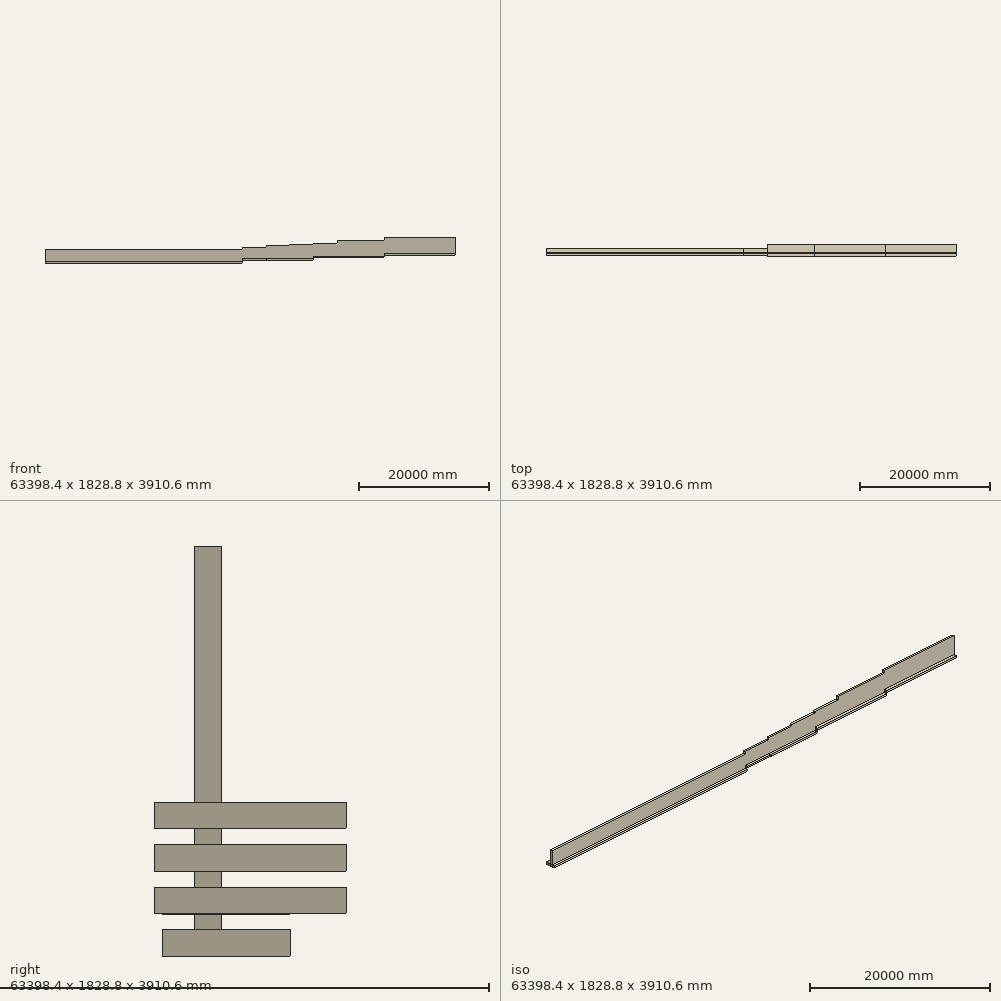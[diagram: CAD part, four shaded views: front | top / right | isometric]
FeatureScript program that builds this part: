
annotation { "Feature Type Name" : "Feature", "Feature Type Description" : "" }
export const myFeature = defineFeature(function(context is Context, id is Id, definition is map)
    precondition{}
    {
        {
            var Q0;
            Q0=qCreatedBy(makeId("Front.planeOp"),FACE);
            var sketch = newSketch(context, id + "F0", { "sketchPlane" : qUnion([Q0])});
            skLineSegment(sketch, "E0.bottom", {"start": v(0, 0) * mm, "end": v(-10972.8, 0) * mm});
            skLineSegment(sketch, "E0.top", {"start": v(0, 2438.4) * mm, "end": v(-10972.8, 2438.4) * mm});
            skLineSegment(sketch, "E0.left", {"start": v(0, 0) * mm, "end": v(0, 2438.4) * mm});
            skLineSegment(sketch, "E0.right", {"start": v(-10972.8, 0) * mm, "end": v(-10972.8, 2438.4) * mm});
            skPoint(sketch, "E1", {"position": v(0, 333.7) * mm});
            skPoint(sketch, "E2", {"position": v(-10972.8, 152.4) * mm});
            skLineSegment(sketch, "E3", {"start": v(-10972.8, 152.4) * mm, "end": v(0, 333.7) * mm, "construction": true});
            skPoint(sketch, "E4", {"position": v(-10972.8, -405.38) * mm});
            skLineSegment(sketch, "E5.left", {"start": v(-10972.8, -405.38) * mm, "end": v(-10972.8, 2033.02) * mm});
            skPoint(sketch, "E6", {"position": v(-33680.4, -643.13) * mm});
            skLineSegment(sketch, "E7", {"start": v(-33680.4, -643.13) * mm, "end": v(-10972.8, 152.4) * mm, "construction": true});
            skPoint(sketch, "E8", {"position": v(-43891.2, -871.73) * mm});
            skLineSegment(sketch, "E9", {"start": v(-43891.2, -871.73) * mm, "end": v(-33680.4, -643.13) * mm, "construction": true});
            skPoint(sketch, "E10", {"position": v(-51511.2, -990.6) * mm});
            skLineSegment(sketch, "E11", {"start": v(-51511.2, -990.6) * mm, "end": v(-43891.2, -871.73) * mm, "construction": true});
            skLineSegment(sketch, "E12.bottom", {"start": v(-51511.2, -990.6) * mm, "end": v(-63398.4, -990.6) * mm, "construction": true});
            skLineSegment(sketch, "E13.bottom", {"start": v(-63398.4, -990.6) * mm, "end": v(-62788.8, -990.6) * mm});
            skPoint(sketch, "E14", {"position": v(-63398.4, 612.65) * mm});
            skPoint(sketch, "E15", {"position": v(-33680.4, 615.7) * mm});
            skLineSegment(sketch, "E16", {"start": v(-63398.4, 612.65) * mm, "end": v(-33680.4, 615.7) * mm, "construction": true});
            skPoint(sketch, "E17", {"position": v(-21945.6, -232.02) * mm});
            skPoint(sketch, "E18", {"position": v(-21945.6, -810.77) * mm});
            skLineSegment(sketch, "E19.bottom", {"start": v(-21945.6, -810.77) * mm, "end": v(-32918.4, -810.77) * mm});
            skPoint(sketch, "E20", {"position": v(-25755.66, 1227.03) * mm});
            skLineSegment(sketch, "E21", {"start": v(-33680.4, 615.7) * mm, "end": v(-25755.66, 1227.03) * mm, "construction": true});
            skPoint(sketch, "E22", {"position": v(-18440.4, 1633.73) * mm});
            skLineSegment(sketch, "E23", {"start": v(-25755.66, 1227.03) * mm, "end": v(-18440.4, 1633.73) * mm, "construction": true});
            skPoint(sketch, "E24", {"position": v(-11125.2, 2039.11) * mm});
            skLineSegment(sketch, "E25", {"start": v(-18440.4, 1633.73) * mm, "end": v(-11125.2, 2039.11) * mm, "construction": true});
            skLineSegment(sketch, "E26", {"start": v(-11125.2, 2039.11) * mm, "end": v(0, 2438.4) * mm, "construction": true});
            skPoint(sketch, "E27", {"position": v(-32918.4, -1216.15) * mm});
            skLineSegment(sketch, "E28.bottom", {"start": v(-32918.4, -1216.15) * mm, "end": v(-63398.4, -1216.15) * mm});
            skLineSegment(sketch, "E28.top", {"start": v(-32918.4, 612.65) * mm, "end": v(-63398.4, 612.65) * mm});
            skLineSegment(sketch, "E28.left", {"start": v(-32918.4, -1216.15) * mm, "end": v(-32918.4, 612.65) * mm});
            skLineSegment(sketch, "E28.right", {"start": v(-63398.4, -1216.15) * mm, "end": v(-63398.4, 612.65) * mm});
            skLineSegment(sketch, "E29.bottom", {"start": v(-10972.8, 2033.02) * mm, "end": v(-18288, 2033.02) * mm});
            skLineSegment(sketch, "E29.top", {"start": v(-10972.8, -405.38) * mm, "end": v(-18288, -405.38) * mm});
            skLineSegment(sketch, "E29.left", {"start": v(-10972.8, 2033.02) * mm, "end": v(-10972.8, -405.38) * mm});
            skLineSegment(sketch, "E29.right", {"start": v(-18288, 2033.02) * mm, "end": v(-18288, -405.38) * mm});
            skLineSegment(sketch, "E30.bottom", {"start": v(-18288, -405.38) * mm, "end": v(-21945.6, -405.38) * mm});
            skLineSegment(sketch, "E30.top", {"start": v(-18288, 1633.73) * mm, "end": v(-21945.6, 1633.73) * mm});
            skLineSegment(sketch, "E30.left", {"start": v(-18288, -405.38) * mm, "end": v(-18288, 1633.73) * mm});
            skLineSegment(sketch, "E30.right", {"start": v(-21945.6, -405.38) * mm, "end": v(-21945.6, 1633.73) * mm});
            skLineSegment(sketch, "E31.right", {"start": v(-21945.6, -809.83) * mm, "end": v(-21945.6, 1438.85) * mm});
            skLineSegment(sketch, "E32.bottom", {"start": v(-21945.6, 1438.85) * mm, "end": v(-25603.2, 1438.85) * mm});
            skLineSegment(sketch, "E32.top", {"start": v(-21945.6, -810.77) * mm, "end": v(-25603.2, -810.77) * mm});
            skLineSegment(sketch, "E32.left", {"start": v(-21945.6, 1438.85) * mm, "end": v(-21945.6, -810.77) * mm});
            skLineSegment(sketch, "E32.right", {"start": v(-25603.2, 1438.85) * mm, "end": v(-25603.2, -810.77) * mm});
            skLineSegment(sketch, "E33.bottom", {"start": v(-25603.2, 1235.5) * mm, "end": v(-29260.8, 1235.5) * mm});
            skLineSegment(sketch, "E33.top", {"start": v(-25603.2, -810.77) * mm, "end": v(-29260.8, -810.77) * mm});
            skLineSegment(sketch, "E33.left", {"start": v(-25603.2, 1235.5) * mm, "end": v(-25603.2, -810.77) * mm});
            skLineSegment(sketch, "E33.right", {"start": v(-29260.8, 1235.5) * mm, "end": v(-29260.8, -810.77) * mm});
            skLineSegment(sketch, "E34.bottom", {"start": v(-29260.8, 956.64) * mm, "end": v(-32918.4, 956.64) * mm});
            skLineSegment(sketch, "E34.top", {"start": v(-29260.8, -810.77) * mm, "end": v(-32918.4, -810.77) * mm});
            skLineSegment(sketch, "E34.left", {"start": v(-29260.8, 956.64) * mm, "end": v(-29260.8, -810.77) * mm});
            skLineSegment(sketch, "E34.right", {"start": v(-32918.4, 956.64) * mm, "end": v(-32918.4, -810.77) * mm});
            skLineSegment(sketch, "E35", {"start": v(0, 0) * mm, "end": v(0, -252.98) * mm});
            skSolve(sketch);
        }
        {
            var Q0;
            Q0 = qSketchRegion(id + "F0", true);
            extrude(context, id + "F1", {"entities" : qUnion([Q0]), "depth" : 252.98 * mm, "offsetDistance" : 30.48 * mm});
        }
        {
            var Q0;
            Q0=qCreatedBy(makeId("Front.planeOp"),FACE);
            var sketch = newSketch(context, id + "F2", { "sketchPlane" : qUnion([Q0])});
            skLineSegment(sketch, "E36.bottom", {"start": v(0, 0) * mm, "end": v(-10972.8, 0) * mm});
            skLineSegment(sketch, "E36.top", {"start": v(0, -252.98) * mm, "end": v(-10972.8, -252.98) * mm});
            skLineSegment(sketch, "E36.left", {"start": v(0, 0) * mm, "end": v(0, -252.98) * mm});
            skLineSegment(sketch, "E36.right", {"start": v(-10972.8, 0) * mm, "end": v(-10972.8, -252.98) * mm});
            skLineSegment(sketch, "E37.bottom", {"start": v(-10972.8, -405.38) * mm, "end": v(-21945.6, -405.38) * mm});
            skLineSegment(sketch, "E37.top", {"start": v(-10972.8, -658.37) * mm, "end": v(-21945.6, -658.37) * mm});
            skLineSegment(sketch, "E37.left", {"start": v(-10972.8, -405.38) * mm, "end": v(-10972.8, -658.37) * mm});
            skLineSegment(sketch, "E37.right", {"start": v(-21945.6, -405.38) * mm, "end": v(-21945.6, -658.37) * mm});
            skPoint(sketch, "E38", {"position": v(-22098, -810.77) * mm});
            skPoint(sketch, "E39", {"position": v(-29413.2, -1063.75) * mm});
            skLineSegment(sketch, "E40.bottom", {"start": v(-29260.8, -1063.75) * mm, "end": v(-21945.6, -1063.75) * mm});
            skLineSegment(sketch, "E40.top", {"start": v(-29260.8, -810.77) * mm, "end": v(-21945.6, -810.77) * mm});
            skLineSegment(sketch, "E40.left", {"start": v(-29260.8, -1063.75) * mm, "end": v(-29260.8, -810.77) * mm});
            skLineSegment(sketch, "E40.right", {"start": v(-21945.6, -1063.75) * mm, "end": v(-21945.6, -810.77) * mm});
            skSolve(sketch);
        }
        {
            var Q0;
            Q0=qCreatedBy(makeId("Front.planeOp"),FACE);
            var sketch = newSketch(context, id + "F3", { "sketchPlane" : qUnion([Q0])});
            skPoint(sketch, "E41", {"position": v(-32918.4, -1219.2) * mm});
            skLineSegment(sketch, "E42.bottom", {"start": v(-32918.4, -1066.8) * mm, "end": v(-29260.8, -1066.8) * mm});
            skLineSegment(sketch, "E42.top", {"start": v(-32918.4, -813.82) * mm, "end": v(-29260.8, -813.82) * mm});
            skLineSegment(sketch, "E42.left", {"start": v(-32918.4, -1066.8) * mm, "end": v(-32918.4, -813.82) * mm});
            skLineSegment(sketch, "E42.right", {"start": v(-29260.8, -1066.8) * mm, "end": v(-29260.8, -813.82) * mm});
            skPoint(sketch, "E43", {"position": v(-32918.4, -813.82) * mm});
            skPoint(sketch, "E44", {"position": v(-63398.4, -1472.18) * mm});
            skLineSegment(sketch, "E45.bottom", {"start": v(-63398.4, -1472.18) * mm, "end": v(-32918.4, -1472.18) * mm});
            skLineSegment(sketch, "E45.top", {"start": v(-63398.4, -1219.2) * mm, "end": v(-32918.4, -1219.2) * mm});
            skLineSegment(sketch, "E45.left", {"start": v(-63398.4, -1472.18) * mm, "end": v(-63398.4, -1219.2) * mm});
            skLineSegment(sketch, "E45.right", {"start": v(-32918.4, -1472.18) * mm, "end": v(-32918.4, -1219.2) * mm});
            skSolve(sketch);
        }
        {
            var Q0;
            Q0 = qSketchRegion(id + "F2", true);
            extrude(context, id + "F4", {"entities" : qUnion([Q0]), "depth" : 633.98 * mm, "hasOffset" : true, "offsetDistance" : 633.98 * mm, "hasSecondDirection" : true, "secondDirectionOppositeDirection" : true, "secondDirectionDepth" : 1194.82 * mm});
        }
        {
            var Q0;
            Q0 = qSketchRegion(id + "F3", true);
            extrude(context, id + "F5", {"entities" : qUnion([Q0]), "depth" : 557.78 * mm, "offsetDistance" : 30.48 * mm, "hasSecondDirection" : true, "secondDirectionOppositeDirection" : true, "secondDirectionDepth" : 661.42 * mm});
        }
    });
